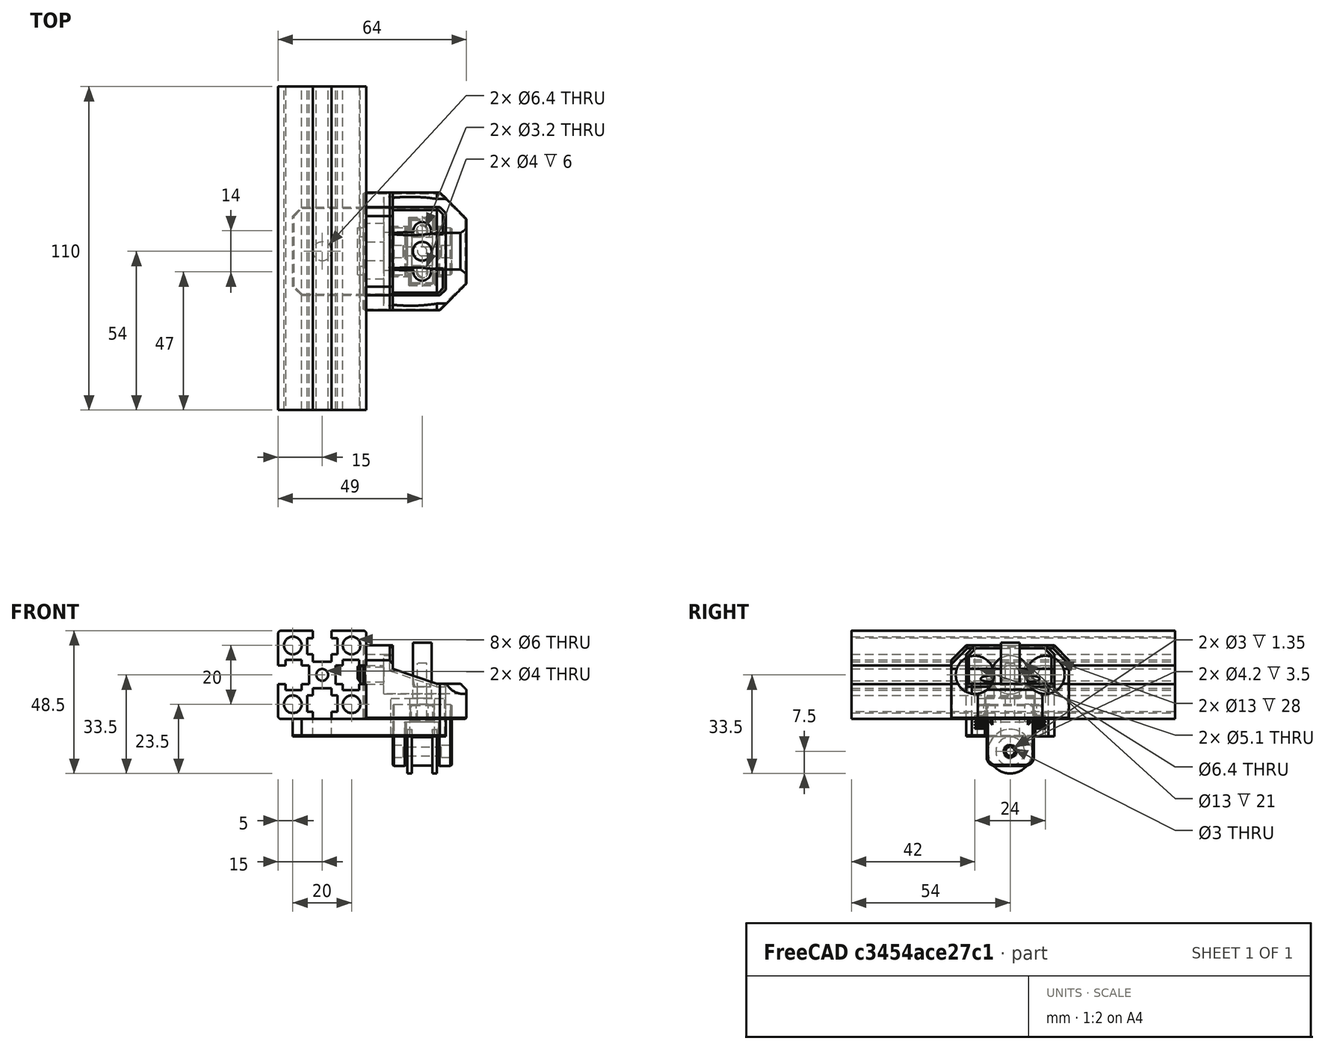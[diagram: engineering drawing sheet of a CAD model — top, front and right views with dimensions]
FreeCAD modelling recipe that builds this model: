
FCSTD DOCUMENT  (FreeCAD 0.18R16146 (Git))
Label: mini-z-belt-idler
License: All rights reserved
LicenseURL: http://en.wikipedia.org/wiki/All_rights_reserved
objects: Part::Cylinder×20, Part::Chamfer×17, Part::MultiFuse×15, Part::Box×14, Part::Cut×10, Part::Feature×9, Part::Fillet×3
note: 88 computed .brp shape members not serialized (recipe doc carries the construction recipe); baked Part::Feature solids carry a one-line shape summary decoded from their .brp

FEATURE [Part::Cylinder] Cylinder
  Angle = 360
  AttacherType = Attacher::AttachEngine3D
  Height = 10
  Radius = 4.84
FEATURE [Part::Cylinder] Cylinder001
  Angle = 360
  AttacherType = Attacher::AttachEngine3D
  Height = 1.5
  Placement = pos=(0,0,8.5) rot=(0,0,1;0rad)
  Radius = 7.5
FEATURE [Part::Cylinder] Cylinder002
  Angle = 360
  AttacherType = Attacher::AttachEngine3D
  Height = 1.5
  Radius = 7.5
FEATURE [Part::Cylinder] Cylinder003
  Angle = 360
  AttacherType = Attacher::AttachEngine3D
  Height = 10
  Radius = 1.5
FEATURE [Part::MultiFuse] Fusion
  Shapes = -> [Cylinder002,Cylinder001,Cylinder]
FEATURE [Part::Cut] Cut  label="16-teeth-idler"
  Base = -> Fusion
  Placement = pos=(-5,0,-11) rot=(0,1,0;1.5708rad)
  Tool = -> Cylinder003
FEATURE [Part::Box] Box  label="Cube"
  AttacherType = Attacher::AttachEngine3D
  Height = 15
  Length = 4.5
  Placement = pos=(5.5,-8,0) rot=(0,0,1;0rad)
  Width = 16
FEATURE [Part::Box] Box001  label="Cube001"
  AttacherType = Attacher::AttachEngine3D
  Height = 15
  Length = 4.5
  Placement = pos=(-10,-8,0) rot=(0,0,1;0rad)
  Width = 16
FEATURE [Part::Box] Box002  label="Cube002"
  AttacherType = Attacher::AttachEngine3D
  Height = 6
  Length = 20
  Placement = pos=(-10,-8,15) rot=(0,0,1;0rad)
  Width = 16
FEATURE [Part::Feature] Fusion041004001  label="_3030-extrusion-002"
  Placement = pos=(-19,0,0) rot=(0,0,1;0rad)
  shape: bbox 30 x 110 x 30 mm, 124 faces (baked)
FEATURE [Part::Cylinder] Cylinder004
  Angle = 360
  AttacherType = Attacher::AttachEngine3D
  Height = 20
  Placement = pos=(-10,0,5) rot=(0,1,0;1.5708rad)
  Radius = 1.5
FEATURE [Part::Cylinder] Cylinder005
  Angle = 360
  AttacherType = Attacher::AttachEngine3D
  Height = 1
  Placement = pos=(5.15,0,5) rot=(0,1,0;1.5708rad)
  Radius = 2.5
FEATURE [Part::Cylinder] Cylinder006
  Angle = 360
  AttacherType = Attacher::AttachEngine3D
  Height = 1
  Placement = pos=(-6.15,0,5) rot=(0,1,0;1.5708rad)
  Radius = 2.5
FEATURE [Part::Chamfer] Chamfer
  Base = -> Cylinder006
  Edges = 1 edges r=0.35: [Edge1]
FEATURE [Part::Chamfer] Chamfer001
  Base = -> Cylinder005
  Edges = 1 edges r=0.35: [Edge3]
FEATURE [Part::Box] Box003  label="Cube003"
  AttacherType = Attacher::AttachEngine3D
  Height = 13
  Length = 21.4
  Placement = pos=(-10.7,-8.2,-6) rot=(0,0,1;0rad)
  Width = 16.4
FEATURE [Part::MultiFuse] Fusion041004003
  Shapes = -> [Chamfer,Chamfer001]
FEATURE [Part::Box] Box004  label="Cube004"
  AttacherType = Attacher::AttachEngine3D
  Height = 25
  Length = 9
  Placement = pos=(-19,-15,0) rot=(0,0,1;0rad)
  Width = 30
FEATURE [Part::Box] Box005  label="Cube005"
  AttacherType = Attacher::AttachEngine3D
  Height = 6
  Length = 30
  Placement = pos=(-44,-15,-6) rot=(0,0,1;0rad)
  Width = 30
FEATURE [Part::Box] Box006  label="Cube006"
  AttacherType = Attacher::AttachEngine3D
  Height = 18
  Length = 22
  Placement = pos=(-14,-15,-6) rot=(0,0,1;0rad)
  Width = 30
FEATURE [Part::Cylinder] Cylinder008
  Angle = 360
  AttacherType = Attacher::AttachEngine3D
  Height = 27
  Placement = pos=(-13,0,15) rot=(0,1,0;1.5708rad)
  Radius = 6.5
FEATURE [Part::Box] Box007  label="Cube007"
  AttacherType = Attacher::AttachEngine3D
  Height = 6
  Length = 8
  Placement = pos=(-4,5,15) rot=(0,0,1;0rad)
  Width = 5
FEATURE [Part::Box] Box008  label="Cube008"
  AttacherType = Attacher::AttachEngine3D
  Height = 6
  Length = 8
  Placement = pos=(-4,-10,15) rot=(0,0,1;0rad)
  Width = 5
FEATURE [Part::Box] Box009  label="Cube009"
  AttacherType = Attacher::AttachEngine3D
  Height = 13
  Length = 8.4
  Placement = pos=(-4.2,-11.2,-6) rot=(0,0,1;0rad)
  Width = 22.4
FEATURE [Part::Cylinder] Cylinder009
  Angle = 360
  AttacherType = Attacher::AttachEngine3D
  Height = 27
  Placement = pos=(-21,0,15) rot=(0,1,0;1.5708rad)
  Radius = 3.2
FEATURE [Part::Cylinder] Cylinder010
  Angle = 360
  AttacherType = Attacher::AttachEngine3D
  Height = 10
  Placement = pos=(-34,0,-10) rot=(0,0,1;0rad)
  Radius = 3.2
FEATURE [Part::Cylinder] Cylinder012
  Angle = 360
  AttacherType = Attacher::AttachEngine3D
  Height = 19
  Radius = 1.6
FEATURE [Part::Cylinder] Cylinder013
  Angle = 360
  AttacherType = Attacher::AttachEngine3D
  Height = 19
  Placement = pos=(0,0,7) rot=(0,0,1;0rad)
  Radius = 3.2
FEATURE [Part::Box] Box010  label="Cube010"
  AttacherType = Attacher::AttachEngine3D
  Height = 6
  Length = 3
  Placement = pos=(-21,-15,12) rot=(0,0,1;0rad)
  Width = 10
FEATURE [Part::Box] Box011  label="Cube011"
  AttacherType = Attacher::AttachEngine3D
  Height = 6
  Length = 3
  Placement = pos=(-21,5,12) rot=(0,0,1;0rad)
  Width = 10
FEATURE [Part::MultiFuse] Fusion041004009  label="aligner"
  Shapes = -> [Box011,Box010]
FEATURE [Part::Feature] Fusion020006007004  label="PREF"
  Placement = pos=(5,0,0) rot=(0,0,1;0rad)
  shape: bbox 37 x 40 x 25 mm, 55 faces (baked)
FEATURE [Part::Fillet] Fillet
  Base = -> Box
  Edges = 2 edges r=3: [Edge9,Edge11]
FEATURE [Part::Fillet] Fillet001
  Base = -> Box001
  Edges = 2 edges r=3: [Edge9,Edge11]
FEATURE [Part::Fillet] Fillet002
  Base = -> Box002
  Edges = 2 edges r=1: [Edge10,Edge12]
FEATURE [Part::Chamfer] Chamfer010
  Base = -> Fillet
  Edges = 5 edges r=0.4: [Edge1,Edge2,Edge4,Edge5,Edge6]
FEATURE [Part::Chamfer] Chamfer011
  Base = -> Fillet001
  Edges = 5 edges r=0.4: [Edge7,Edge11,Edge15,Edge16,Edge18]
FEATURE [Part::Cylinder] Cylinder014
  Angle = 360
  AttacherType = Attacher::AttachEngine3D
  Height = 3.5
  Placement = pos=(-10,0,5) rot=(0,1,0;1.5708rad)
  Radius = 2.1
FEATURE [Part::Cylinder] Cylinder015
  Angle = 360
  AttacherType = Attacher::AttachEngine3D
  Height = 3.5
  Placement = pos=(6.5,0,5) rot=(0,1,0;1.5708rad)
  Radius = 2.1
FEATURE [Part::MultiFuse] Fusion020006007006
  Shapes = -> [Cylinder015,Cylinder014]
FEATURE [Part::Chamfer] Chamfer013
  Base = -> Box004
  Edges = 2 edges r=3: [Edge10,Edge12]
FEATURE [Part::MultiFuse] Fusion020006007008
  Shapes = -> [Chamfer013,Box006,Box005,Fusion041004009]
FEATURE [Part::Chamfer] Chamfer014
  Base = -> Fusion020006007008
  Edges = 1 edges: [Edge13 r1=15 r2=5]
FEATURE [Part::MultiFuse] Fusion020006007009
  Shapes = -> [Cylinder009,Cylinder008]
FEATURE [Part::Cylinder] Cylinder016
  Angle = 360
  AttacherType = Attacher::AttachEngine3D
  Height = 20
  Placement = pos=(0,-7,11) rot=(0,0,1;0rad)
  Radius = 3
FEATURE [Part::Cylinder] Cylinder017
  Angle = 360
  AttacherType = Attacher::AttachEngine3D
  Height = 20
  Placement = pos=(0,7,11) rot=(0,0,1;0rad)
  Radius = 3
FEATURE [Part::Chamfer] Chamfer015
  Base = -> Box008
  Edges = 12 edges r=0.4: [Edge1,Edge2,Edge3,Edge4,Edge5,Edge6,Edge7,Edge8,Edge9,Edge10,Edge11,Edge12]
  Placement = pos=(0,-1,0) rot=(0,0,1;0rad)
FEATURE [Part::Chamfer] Chamfer016
  Base = -> Box007
  Edges = 11 edges r=0.4: [Edge1,Edge2,Edge3,Edge4,Edge5,Edge6,Edge7,Edge8,Edge10,Edge11,Edge12]
  Placement = pos=(0,1,0) rot=(0,0,1;0rad)
FEATURE [Part::Chamfer] Chamfer017
  Base = -> Chamfer010
  Edges = 5 edges r=0.4: [Edge22,Edge24,Edge25,Edge26,Edge27]
FEATURE [Part::Chamfer] Chamfer018
  Base = -> Chamfer011
  Edges = 5 edges r=0.4: [Edge3,Edge6,Edge12,Edge13,Edge14]
FEATURE [Part::Chamfer] Chamfer019
  Base = -> Fillet002
  Edges = 10 edges r=0.4: [Edge1,Edge2,Edge4,Edge5,Edge6,Edge7,Edge11,Edge15,Edge16,Edge18]
FEATURE [Part::Cylinder] Cylinder018
  Angle = 360
  AttacherType = Attacher::AttachEngine3D
  Height = 20
  Placement = pos=(0,-7,12) rot=(0,0,1;0rad)
  Radius = 2
FEATURE [Part::Cylinder] Cylinder019
  Angle = 360
  AttacherType = Attacher::AttachEngine3D
  Height = 20
  Placement = pos=(0,7,12) rot=(0,0,1;0rad)
  Radius = 2
FEATURE [Part::Cylinder] Cylinder020
  Angle = 360
  AttacherType = Attacher::AttachEngine3D
  Height = 20
  Placement = pos=(0,-7,2) rot=(0,0,1;0rad)
  Radius = 1.6
FEATURE [Part::Cylinder] Cylinder021
  Angle = 360
  AttacherType = Attacher::AttachEngine3D
  Height = 20
  Placement = pos=(0,7,2) rot=(0,0,1;0rad)
  Radius = 1.6
FEATURE [Part::MultiFuse] Fusion020006007013
  Shapes = -> [Cylinder018,Cylinder019]
FEATURE [Part::MultiFuse] Fusion020006007012
  Shapes = -> [Chamfer019,Chamfer015,Chamfer016]
FEATURE [Part::MultiFuse] Fusion020006007014
  Shapes = -> [Chamfer017,Fusion020006007012,Chamfer018]
FEATURE [Part::Cut] Cut009006
  Base = -> Fusion020006007014
  Tool = -> Fusion020006007013
FEATURE [Part::MultiFuse] Fusion020006007015
  Shapes = -> [Fusion041004003,Cut009006]
FEATURE [Part::Cut] Cut009007
  Base = -> Fusion020006007015
  Tool = -> Cylinder004
FEATURE [Part::Cut] Cut009008
  Base = -> Cut009007
  Placement = pos=(0,0,-16) rot=(0,0,1;0rad)
  Tool = -> Fusion020006007006
FEATURE [Part::MultiFuse] Fusion020006007016
  Shapes = -> [Box009,Box003]
FEATURE [Part::Cut] Cut009009
  Base = -> Chamfer014
  Tool = -> Fusion020006007016
FEATURE [Part::MultiFuse] Fusion020006007017
  Shapes = -> [Cylinder021,Cylinder020,Cylinder017,Cylinder016]
FEATURE [Part::Chamfer] Chamfer020
  Base = -> Cut009009
  Edges = 2 edges r=2: [Edge3,Edge22]
FEATURE [Part::Chamfer] Chamfer021
  Base = -> Chamfer020
  Edges = 2 edges r=3: [Edge44,Edge99]
FEATURE [Part::Cut] Cut009010
  Base = -> Chamfer021
  Tool = -> Cylinder010
FEATURE [Part::Feature] Cut009010001  label="Cut009011"
  shape: bbox 52 x 30 x 31 mm, 38 faces (baked)
FEATURE [Part::Chamfer] Chamfer022
  Base = -> Cut009010001
  Edges = 12 edges r=1: [Edge32,Edge33,Edge34,Edge36,Edge37,Edge38,Edge42,Edge44,Edge45,Edge46,Edge47,Edge48]
FEATURE [Part::Chamfer] Chamfer023
  Base = -> Chamfer022
  Edges = 21 edges r=0.4: [Edge7,Edge34,Edge39,Edge40,Edge41,Edge44,Edge45,Edge46,Edge47,Edge48,Edge49,Edge50,Edge51,Edge52,Edge53,Edge54,Edge55,Edge56,Edge96,Edge97,Edge98]
FEATURE [Part::Cut] Cut009010002
  Base = -> Chamfer023
  Tool = -> Fusion020006007009
FEATURE [Part::Cut] Cut009010003
  Base = -> Cut009010002
  Tool = -> Fusion020006007017
FEATURE [Part::Feature] Box012001001  label="Cube014"
  Placement = pos=(9,9,-1) rot=(0,0,1;0rad)
  shape: bbox 2.828 x 3 x 2.828 mm, 6 faces (baked)
FEATURE [Part::Feature] Box012001002  label="Cube015"
  Placement = pos=(9,-12,-1) rot=(0,0,1;0rad)
  shape: bbox 2.828 x 3 x 2.828 mm, 6 faces (baked)
FEATURE [Part::MultiFuse] Fusion020006007018
  Shapes = -> [Box012001002,Box012001001]
FEATURE [Part::Feature] Fusion020006007018001  label="Fusion020006007019"
  Placement = pos=(0,0,1) rot=(0,0,1;0rad)
  shape: bbox 2.828 x 24 x 2.828 mm, 12 faces, 2 solids (baked)
FEATURE [Part::Feature] Fusion020006007018002  label="Fusion020006007020"
  Placement = pos=(0,0,2) rot=(0,0,1;0rad)
  shape: bbox 2.828 x 24 x 2.828 mm, 12 faces, 2 solids (baked)
FEATURE [Part::Feature] Fusion020006007018003  label="Fusion020006007021"
  Placement = pos=(0,0,-1) rot=(0,0,1;0rad)
  shape: bbox 2.828 x 24 x 2.828 mm, 12 faces, 2 solids (baked)
FEATURE [Part::Feature] Fusion020006007018004  label="Fusion020006007022"
  Placement = pos=(0,0,-2) rot=(0,0,1;0rad)
  shape: bbox 2.828 x 24 x 2.828 mm, 12 faces, 2 solids (baked)
FEATURE [Part::MultiFuse] Fusion020006007018005
  Placement = pos=(0.2,0,0) rot=(0,0,1;0rad)
  Shapes = -> [Fusion020006007018004,Fusion020006007018003,Fusion020006007018002,Fusion020006007018001,Fusion020006007018]
FEATURE [Part::Cut] Cut009010004
  Base = -> Cut009010003
  Tool = -> Fusion020006007018005
FEATURE [Part::Box] Box012001003  label="Cube016"
  AttacherType = Attacher::AttachEngine3D
  Height = 2
  Length = 1
  Placement = pos=(9.5,-7,-2) rot=(0,0,1;0rad)
  Width = 1
FEATURE [Part::Box] Box012001004  label="Cube017"
  AttacherType = Attacher::AttachEngine3D
  Height = 2
  Length = 1
  Placement = pos=(9.5,6,-2) rot=(0,0,1;0rad)
  Width = 1
FEATURE [Part::Chamfer] Chamfer024
  Base = -> Box012001003
  Edges = 2 edges r=0.99: [Edge9,Edge10]
FEATURE [Part::Chamfer] Chamfer025
  Base = -> Box012001004
  Edges = 2 edges r=0.99: [Edge11,Edge12]
FEATURE [Part::MultiFuse] Fusion020006007018006
  Shapes = -> [Chamfer024,Chamfer025]
FEATURE [Part::Cut] Cut009010005
  Base = -> Cut009008
  Tool = -> Fusion020006007018006
